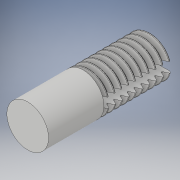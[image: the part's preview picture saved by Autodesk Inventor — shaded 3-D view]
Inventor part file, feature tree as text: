
AUTODESK INVENTOR PART (.ipt)
format: ipt  version: 2019 (Build 230136000, 136)  size: 885,248 bytes
history: native  units: mm
features: sketch x5, extrude x2, revolve x2, thread x1, helix x1, boolean_combine x1
ambient origin geometry x8: Origin, YZ Plane, XZ Plane, XY Plane, X Axis, Y Axis, Z Axis, Center Point
bodies: Solid1 (feature_tree), Solid2 (feature_tree)
feature tree (12):
  extrude  "Extrusion1"  Depth=18.1mm TaperAngle=0.0deg
  thread  "Thread1"  [1 undecoded]
  revolve  "Revolution1"  [1 undecoded]
  revolve  "Revolution2"  [1 undecoded]
  helix  "Coil1"  [1 undecoded]
  sketch  "Sketch5"  dims[d25=10.0mm d26=0.0mm d27=8.0mm]
  boolean_combine  "Combine1"
  extrude  "Extrusion2"  Depth=1.5mm
  sketch  "Sketch1"  dims[d0=6.1mm d1=18.1mm d2=0.0mm d3=10.0mm d4=0.0mm]
  sketch  "Sketch2"  dims[d5=9.599311mm d6=0.160083mm d7=0.160083mm d10=1.0mm]
  sketch  "Sketch3"  dims[d12=9.599311mm d14=0.0mm d15=0.0mm]
  sketch  "Sketch4"  dims[d16=1.001mm d17=12.0mm d18=10.0mm d19=0.0mm d20=0.0mm d21=0.0mm d22=0.0mm d23=0.0mm d24=1.5mm]
note: 4 required parameter values undecoded (feature->parameter linkage not recoverable at this tier; creation-order binding heuristic only, values carry confidence <= 0.55)